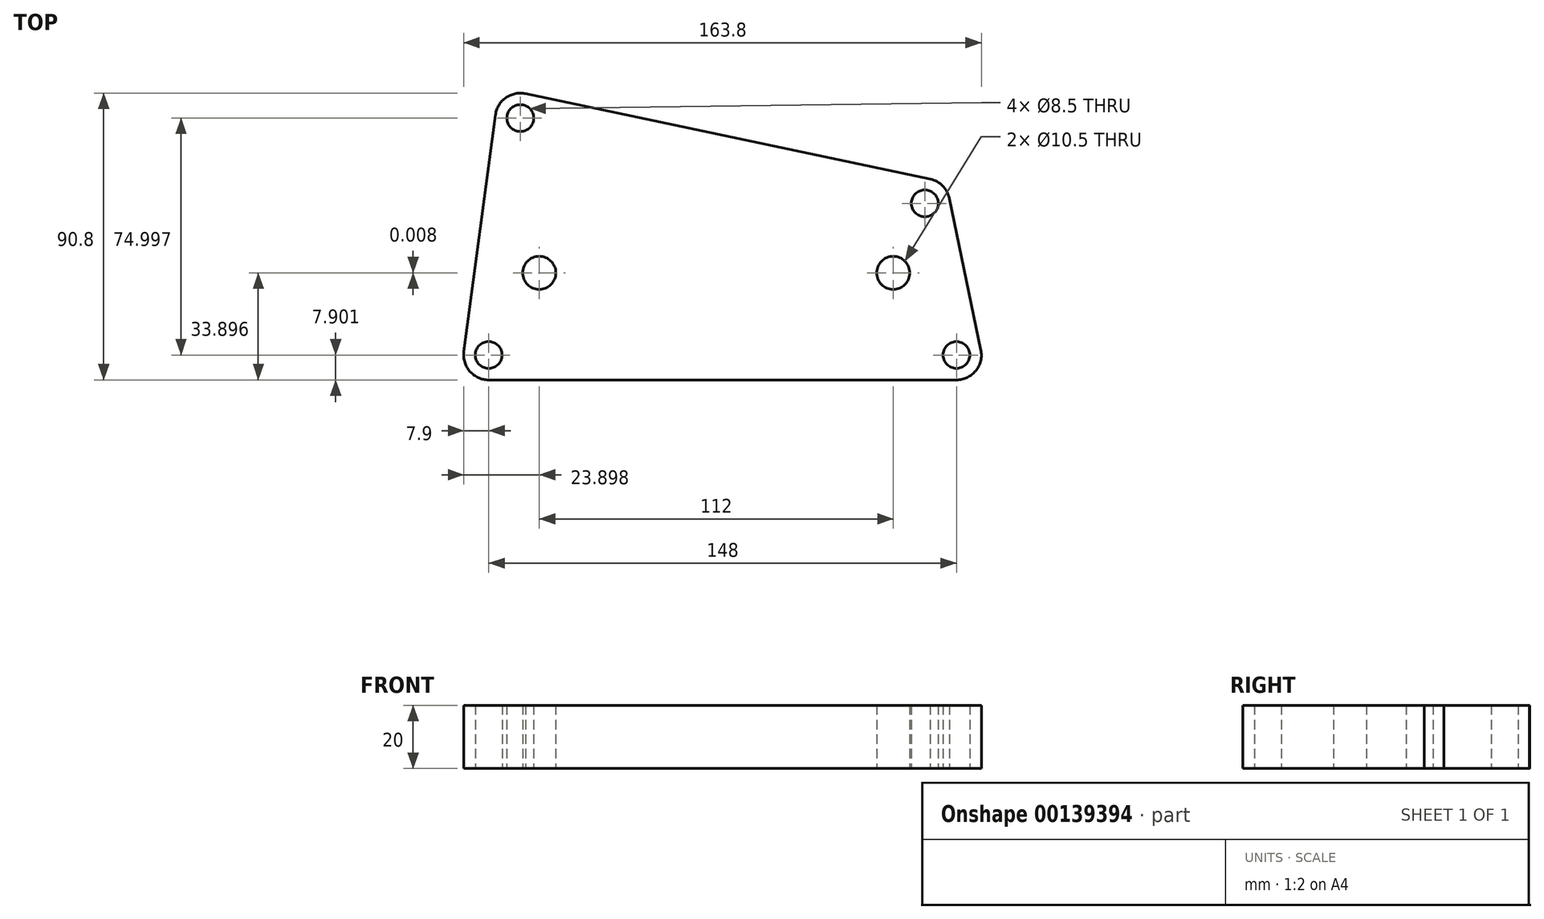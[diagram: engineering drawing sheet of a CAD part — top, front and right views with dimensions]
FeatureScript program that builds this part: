
annotation { "Feature Type Name" : "Feature", "Feature Type Description" : "" }
export const myFeature = defineFeature(function(context is Context, id is Id, definition is map)
    precondition{}
    {
        {
            var Q0;
            Q0=qCreatedBy(makeId("Top.planeOp"),FACE);
            var sketch = newSketch(context, id + "F0", { "sketchPlane" : qUnion([Q0])});
            skCircle(sketch, "E0", {"center": v(-195.99, -17.23) * mm, "radius": 4.25 * mm});
            skCircle(sketch, "E1", {"center": v(-47.99, -17.23) * mm, "radius": 4.25 * mm});
            skCircle(sketch, "E2", {"center": v(-57.99, 30.77) * mm, "radius": 4.25 * mm});
            skCircle(sketch, "E3", {"center": v(-186, 57.77) * mm, "radius": 4.25 * mm});
            skArc(sketch, "E4", {"start": v(-203.82, -16.19) * mm, "mid": v(-201.93, -22.43) * mm, "end": v(-195.99, -25.13) * mm});
            skArc(sketch, "E5", {"start": v(-50.24, 32.29) * mm, "mid": v(-52.33, 36.28) * mm, "end": v(-56.26, 38.48) * mm});
            skArc(sketch, "E6", {"start": v(-47.99, -25.13) * mm, "mid": v(-41.86, -22.21) * mm, "end": v(-40.26, -15.62) * mm});
            skLineSegment(sketch, "E7", {"start": v(-184.27, 65.48) * mm, "end": v(-121.2, 52.17) * mm});
            skLineSegment(sketch, "E8", {"start": v(-56.26, 38.48) * mm, "end": v(-121.2, 52.17) * mm});
            skLineSegment(sketch, "E9", {"start": v(-193.82, 58.81) * mm, "end": v(-203.82, -16.19) * mm});
            skLineSegment(sketch, "E10", {"start": v(-195.99, -25.13) * mm, "end": v(-47.99, -25.13) * mm});
            skLineSegment(sketch, "E11", {"start": v(-50.24, 32.29) * mm, "end": v(-40.26, -15.62) * mm});
            skArc(sketch, "E12.trimOffspring", {"start": v(-184.27, 65.48) * mm, "mid": v(-190.51, 64.25) * mm, "end": v(-193.82, 58.81) * mm});
            skCircle(sketch, "E13", {"center": v(-180, 8.77) * mm, "radius": 5.25 * mm});
            skCircle(sketch, "E14", {"center": v(-68, 8.77) * mm, "radius": 5.25 * mm});
            skSolve(sketch);
        }
        {
            var Q0;
            Q0 = qSketchRegion(id + "F0", true);
            extrude(context, id + "F1", {"entities" : qUnion([Q0]), "depth" : 20 * mm});
        }
    });
